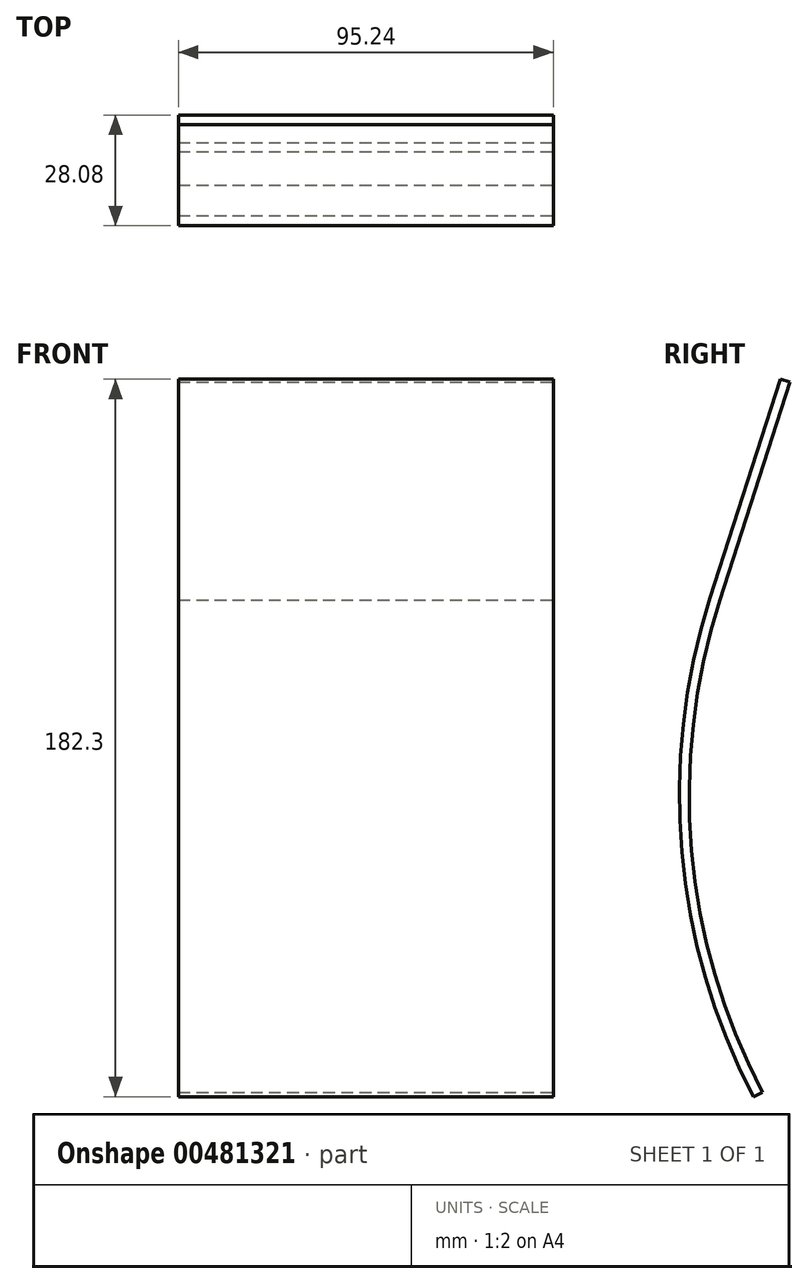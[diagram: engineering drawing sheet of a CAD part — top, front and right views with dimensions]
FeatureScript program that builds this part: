
annotation { "Feature Type Name" : "Feature", "Feature Type Description" : "" }
export const myFeature = defineFeature(function(context is Context, id is Id, definition is map)
    precondition{}
    {
        {
            var Q0;
            Q0=qCreatedBy(makeId("Right.planeOp"),FACE);
            var sketch = newSketch(context, id + "F0", { "sketchPlane" : qUnion([Q0])});
            skLineSegment(sketch, "E0", {"start": v(122.12, 51.37) * mm, "end": v(-90.12, 90.98) * mm});
            skLineSegment(sketch, "E1", {"start": v(-90.12, 90.98) * mm, "end": v(-67.72, -59.76) * mm});
            skLineSegment(sketch, "E2", {"start": v(122.12, 51.37) * mm, "end": v(122.12, -43.88) * mm});
            skLineSegment(sketch, "E3", {"start": v(-67.72, -59.76) * mm, "end": v(122.12, -43.88) * mm});
            skCircle(sketch, "E4", {"center": v(90.37, 36.36) * mm, "radius": 3.18 * mm});
            skCircle(sketch, "E5", {"center": v(109.92, 20.05) * mm, "radius": 3.18 * mm});
            skCircle(sketch, "E6", {"center": v(109.92, -34.05) * mm, "radius": 3.18 * mm});
            skSolve(sketch);
        }
        {
            var Q0;
            Q0=qSketchRegion(id+"F0",true);
            var Q1;
            Q1=makeQuery(id+"F0.imprint","IMPRINT",FACE,{"disambiguationData":[TD([[makeQuery(id+"F0.imprint","IMPRINT",EDGE,{"derivedFrom":sQuery(id+"F0.wireOp",EDGE,"E4")}),1.0]])]});
            var Q2;
            Q2=makeQuery(id+"F0.imprint","IMPRINT",FACE,{"disambiguationData":[TD([[makeQuery(id+"F0.imprint","IMPRINT",EDGE,{"derivedFrom":sQuery(id+"F0.wireOp",EDGE,"E5")}),1.0]])]});
            var Q3;
            Q3=makeQuery(id+"F0.imprint","IMPRINT",FACE,{"disambiguationData":[TD([[makeQuery(id+"F0.imprint","IMPRINT",EDGE,{"derivedFrom":sQuery(id+"F0.wireOp",EDGE,"E6")}),1.0]])]});
            extrude(context, id + "F1", {"entities" : qUnion([Q0, Q1, Q2, Q3]), "depth" : 11.43 * mm});
        }
        {
            var Q0;
            Q0=makeQuery(id+"F1.opExtrude","SWEPT_BODY",BODY,{"disambiguationData":[OSD([sQuery(id+"F0.wireOp",EDGE,"E0"),sQuery(id+"F0.wireOp",EDGE,"E1"),sQuery(id+"F0.wireOp",EDGE,"E2"),sQuery(id+"F0.wireOp",EDGE,"E3"),sQuery(id+"F0.wireOp",EDGE,"E4"),sQuery(id+"F0.wireOp",EDGE,"E5"),sQuery(id+"F0.wireOp",EDGE,"E6")])]});
            transform(context, id + "F2", {"entities" : qUnion([Q0]), "transformType" : TransformType.TRANSLATION_3D, "dx" : 47.62 * mm, "dy" : 0 * mm, "dz" : 0 * mm, "makeCopy" : false});
        }
        {
            var Q0;
            Q0=makeQuery(id+"F1.opExtrude","SWEPT_BODY",BODY,{"disambiguationData":[OSD([sQuery(id+"F0.wireOp",EDGE,"E0"),sQuery(id+"F0.wireOp",EDGE,"E1"),sQuery(id+"F0.wireOp",EDGE,"E2"),sQuery(id+"F0.wireOp",EDGE,"E3"),sQuery(id+"F0.wireOp",EDGE,"E4"),sQuery(id+"F0.wireOp",EDGE,"E5"),sQuery(id+"F0.wireOp",EDGE,"E6")])]});
            var Q1;
            Q1=qCreatedBy(makeId("Right.planeOp"),FACE);
            mirror(context, id + "F3", {"entities" : qUnion([Q0]), "mirrorPlane" : qUnion([Q1])});
        }
        {
            var Q0;
            Q0=makeQuery(id+"F3.opPattern","COPY",FACE,{"derivedFrom":makeQuery(id+"F1.opExtrude","CAP_FACE",FACE,{"disambiguationData":[OSD([sQuery(id+"F0.wireOp",EDGE,"E0"),sQuery(id+"F0.wireOp",EDGE,"E1"),sQuery(id+"F0.wireOp",EDGE,"E2"),sQuery(id+"F0.wireOp",EDGE,"E3"),sQuery(id+"F0.wireOp",EDGE,"E4"),sQuery(id+"F0.wireOp",EDGE,"E5"),sQuery(id+"F0.wireOp",EDGE,"E6")])],"isStart":false}),"instanceName":"1"});
            var sketch = newSketch(context, id + "F4", { "sketchPlane" : qUnion([Q0])});
            skLineSegment(sketch, "E7", {"start": v(-122.12, -43.88) * mm, "end": v(-33.22, -43.88) * mm});
            skCircle(sketch, "E8", {"center": v(-33.22, -43.88) * mm, "radius": 50.8 * mm});
            skLineSegment(sketch, "E9", {"start": v(17.58, -43.88) * mm, "end": v(17.58, -55.57) * mm});
            skSolve(sketch);
        }
        {
            var Q0;
            {var subQ0=sQuery(id+"F4.wireOp",EDGE,"E8");var subQ1=makeQuery(id+"F4.imprint","INTERSECT",VERTEX,{"derivedFrom":[subQ0,sQuery(id+"F4.wireOp",EDGE,"E9")]});Q0=makeQuery(id+"F4.imprint","IMPRINT",FACE,{"disambiguationData":[TD([[makeQuery(id+"F4.imprint","IMPRINT",EDGE,{"disambiguationData":[TD([[subQ1,-1.0]])],"derivedFrom":subQ0}),1.0]])]});}
            var Q1;
            {var subQ0=sQuery(id+"F4.wireOp",EDGE,"E9");Q1=makeQuery(id+"F4.imprint","IMPRINT",FACE,{"disambiguationData":[TD([[makeQuery(id+"F4.imprint","IMPRINT",EDGE,{"derivedFrom":subQ0}),-1.0]])]});}
            extrude(context, id + "F5", {"entities" : qUnion([Q0, Q1]), "operationType" : NewBodyOperationType.REMOVE, "oppositeDirection" : true, "depth" : 25.4 * mm});
        }
        {
            var Q0;
            Q0=sQuery(id+"F0.wireOp",VERTEX,"E4.center");
            var Q1;
            Q1=makeQuery(id+"F3.opPattern","COPY",BODY,{"derivedFrom":makeQuery(id+"F1.opExtrude","SWEPT_BODY",BODY,{"disambiguationData":[OSD([sQuery(id+"F0.wireOp",EDGE,"E0"),sQuery(id+"F0.wireOp",EDGE,"E1"),sQuery(id+"F0.wireOp",EDGE,"E2"),sQuery(id+"F0.wireOp",EDGE,"E3")])]}),"instanceName":"1"});
            hole(context, id + "F6", {"style" : HoleStyle.SIMPLE, "endStyle" : HoleEndStyle.BLIND, "holeDiameter" : 6.35 * mm, "holeDepth" : 76.2 * mm, "isTappedThrough" : true, "tappedDepth" : 12.7 * mm, "tapClearance" : 3, "startFromSketch" : true, "locations" : qUnion([Q0]), "scope" : qUnion([Q1])});
        }
        {
            var Q0;
            Q0=sQuery(id+"F0.wireOp",VERTEX,"E5.center");
            var Q1;
            Q1=makeQuery(id+"F3.opPattern","COPY",BODY,{"derivedFrom":makeQuery(id+"F1.opExtrude","SWEPT_BODY",BODY,{"disambiguationData":[OSD([sQuery(id+"F0.wireOp",EDGE,"E0"),sQuery(id+"F0.wireOp",EDGE,"E1"),sQuery(id+"F0.wireOp",EDGE,"E2"),sQuery(id+"F0.wireOp",EDGE,"E3")])]}),"instanceName":"1"});
            hole(context, id + "F7", {"style" : HoleStyle.SIMPLE, "endStyle" : HoleEndStyle.BLIND, "holeDiameter" : 6.35 * mm, "holeDepth" : 76.2 * mm, "isTappedThrough" : true, "tappedDepth" : 12.7 * mm, "tapClearance" : 3, "startFromSketch" : true, "locations" : qUnion([Q0]), "scope" : qUnion([Q1])});
        }
        {
            var Q0;
            Q0=sQuery(id+"F0.wireOp",VERTEX,"E6.center");
            var Q1;
            Q1=makeQuery(id+"F3.opPattern","COPY",BODY,{"derivedFrom":makeQuery(id+"F1.opExtrude","SWEPT_BODY",BODY,{"disambiguationData":[OSD([sQuery(id+"F0.wireOp",EDGE,"E0"),sQuery(id+"F0.wireOp",EDGE,"E1"),sQuery(id+"F0.wireOp",EDGE,"E2"),sQuery(id+"F0.wireOp",EDGE,"E3")])]}),"instanceName":"1"});
            hole(context, id + "F8", {"style" : HoleStyle.SIMPLE, "endStyle" : HoleEndStyle.BLIND, "holeDiameter" : 6.35 * mm, "holeDepth" : 76.2 * mm, "isTappedThrough" : true, "tappedDepth" : 12.7 * mm, "tapClearance" : 3, "startFromSketch" : true, "locations" : qUnion([Q0]), "scope" : qUnion([Q1])});
        }
        {
            var Q0;
            Q0=sQuery(id+"F0.wireOp",VERTEX,"E4.center");
            var Q1;
            Q1=makeQuery(id+"F1.opExtrude","SWEPT_BODY",BODY,{"disambiguationData":[OSD([sQuery(id+"F0.wireOp",EDGE,"E0"),sQuery(id+"F0.wireOp",EDGE,"E1"),sQuery(id+"F0.wireOp",EDGE,"E2"),sQuery(id+"F0.wireOp",EDGE,"E3")])]});
            hole(context, id + "F9", {"style" : HoleStyle.SIMPLE, "endStyle" : HoleEndStyle.BLIND, "oppositeDirection" : true, "holeDiameter" : 6.35 * mm, "holeDepth" : 76.2 * mm, "isTappedThrough" : true, "tappedDepth" : 12.7 * mm, "tapClearance" : 3, "startFromSketch" : true, "locations" : qUnion([Q0]), "scope" : qUnion([Q1])});
        }
        {
            var Q0;
            Q0=makeQuery(id+"F1.opExtrude","CAP_FACE",FACE,{"disambiguationData":[OSD([sQuery(id+"F0.wireOp",EDGE,"E0"),sQuery(id+"F0.wireOp",EDGE,"E1"),sQuery(id+"F0.wireOp",EDGE,"E2"),sQuery(id+"F0.wireOp",EDGE,"E3")])],"isStart":true});
            var sketch = newSketch(context, id + "F10", { "sketchPlane" : qUnion([Q0])});
            skCircle(sketch, "E10", {"center": v(-90.37, 36.36) * mm, "radius": 66.68 * mm});
            skCircle(sketch, "E11.0", {"center": v(-90.37, 36.36) * mm, "radius": 161.93 * mm});
            skCircle(sketch, "E12.0", {"center": v(-90.37, 36.36) * mm, "radius": 164.47 * mm});
            skLineSegment(sketch, "E13", {"start": v(52.96, -38.98) * mm, "end": v(55.23, -40.13) * mm});
            skLineSegment(sketch, "E14", {"start": v(66.26, 86.53) * mm, "end": v(48.44, 142.17) * mm});
            skLineSegment(sketch, "E15", {"start": v(48.44, 142.17) * mm, "end": v(46.02, 141.4) * mm});
            skLineSegment(sketch, "E16", {"start": v(46.02, 141.4) * mm, "end": v(63.74, 86.06) * mm});
            skSolve(sketch);
        }
        {
            var Q0;
            {var subQ0=sQuery(id+"F10.wireOp",EDGE,"E14");Q0=makeQuery(id+"F10.imprint","IMPRINT",FACE,{"disambiguationData":[TD([[makeQuery(id+"F10.imprint","IMPRINT",EDGE,{"derivedFrom":subQ0}),1.0]])]});}
            var Q1;
            {var subQ1=makeQuery(id+"F1.opExtrude","CAP_EDGE",EDGE,{"disambiguationData":[OSD([sQuery(id+"F0.wireOp",EDGE,"E0")])],"isStart":true});var subQ3=sQuery(id+"F10.wireOp",EDGE,"E16");var subQ5=makeQuery(id+"F10.imprint","INTERSECT",VERTEX,{"derivedFrom":[subQ1,subQ3]});Q1=makeQuery(id+"F10.imprint","IMPRINT",FACE,{"disambiguationData":[TD([[makeQuery(id+"F10.imprint","IMPRINT",EDGE,{"disambiguationData":[TD([[subQ5,1.0]])],"derivedFrom":subQ3}),1.0]])]});}
            var Q2;
            {var subQ4=sQuery(id+"F10.wireOp",EDGE,"E13");Q2=makeQuery(id+"F10.imprint","IMPRINT",FACE,{"disambiguationData":[TD([[makeQuery(id+"F10.imprint","IMPRINT",EDGE,{"derivedFrom":subQ4}),1.0]])]});}
            extrude(context, id + "F11", {"entities" : qUnion([Q0, Q1, Q2]), "depth" : 95.25 * mm});
        }
        {
            var Q0;
            Q0=makeQuery(id+"F3.opPattern","COPY",BODY,{"derivedFrom":makeQuery(id+"F1.opExtrude","SWEPT_BODY",BODY,{"disambiguationData":[OSD([sQuery(id+"F0.wireOp",EDGE,"E0"),sQuery(id+"F0.wireOp",EDGE,"E1"),sQuery(id+"F0.wireOp",EDGE,"E2"),sQuery(id+"F0.wireOp",EDGE,"E3")])]}),"instanceName":"1"});
            deleteBodies(context, id + "F12", {"entities" : qUnion([Q0])});
        }
        {
            var Q0;
            Q0=makeQuery(id+"F1.opExtrude","SWEPT_BODY",BODY,{"disambiguationData":[OSD([sQuery(id+"F0.wireOp",EDGE,"E0"),sQuery(id+"F0.wireOp",EDGE,"E1"),sQuery(id+"F0.wireOp",EDGE,"E2"),sQuery(id+"F0.wireOp",EDGE,"E3")])]});
            deleteBodies(context, id + "F13", {"entities" : qUnion([Q0])});
        }
    });
